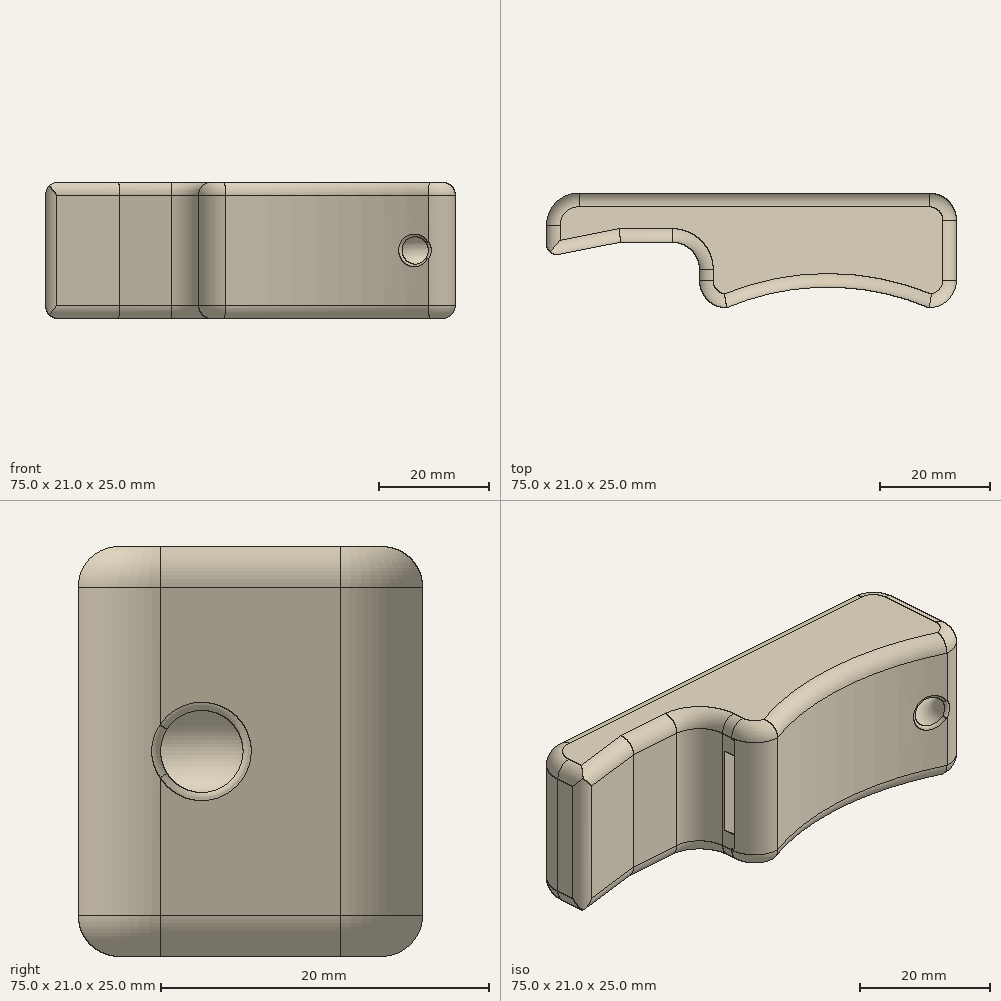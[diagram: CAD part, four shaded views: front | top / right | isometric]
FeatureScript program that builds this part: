
annotation { "Feature Type Name" : "Feature", "Feature Type Description" : "" }
export const myFeature = defineFeature(function(context is Context, id is Id, definition is map)
    precondition{}
    {
        {
            var Q0;
            Q0=qCreatedBy(makeId("Top.planeOp"),FACE);
            var sketch = newSketch(context, id + "F0", { "sketchPlane" : qUnion([Q0])});
            skLineSegment(sketch, "E0", {"start": v(5, -2) * mm, "end": v(5, 0) * mm});
            skPoint(sketch, "E1.visualSharp", {"position": v(0, 0) * mm});
            skArc(sketch, "E1.filletArc", {"start": v(5, 0) * mm, "mid": v(3.54, 3.54) * mm, "end": v(0, 5) * mm});
            skArc(sketch, "E2.filletArc", {"start": v(47, -7) * mm, "mid": v(50.54, -5.54) * mm, "end": v(52, -2) * mm});
            skPoint(sketch, "E3.visualSharp", {"position": v(5, -7) * mm});
            skArc(sketch, "E3.filletArc", {"start": v(5, -2) * mm, "mid": v(6.46, -5.54) * mm, "end": v(10, -7) * mm});
            skLineSegment(sketch, "E4", {"start": v(0, 5) * mm, "end": v(-9.45, 5) * mm});
            skArc(sketch, "E5", {"start": v(-17, 14) * mm, "mid": v(-21.24, 12.24) * mm, "end": v(-23, 8) * mm});
            skLineSegment(sketch, "E6", {"start": v(-23, -19.5) * mm, "end": v(-23, 8) * mm, "construction": true});
            skLineSegment(sketch, "E7", {"start": v(52, -19.5) * mm, "end": v(52, -2) * mm, "construction": true});
            skLineSegment(sketch, "E8", {"start": v(-17, 14) * mm, "end": v(47, 14) * mm});
            skLineSegment(sketch, "E9", {"start": v(52, 9) * mm, "end": v(52, -2) * mm});
            skPoint(sketch, "E10.visualSharp", {"position": v(52, 14) * mm});
            skArc(sketch, "E10.filletArc", {"start": v(52, 9) * mm, "mid": v(50.54, 12.54) * mm, "end": v(47, 14) * mm});
            skArc(sketch, "E11", {"start": v(47, -7) * mm, "mid": v(28.5, -3.21) * mm, "end": v(10, -7) * mm});
            skLineSegment(sketch, "E12", {"start": v(-23, 4.7) * mm, "end": v(-23, 8) * mm});
            skPoint(sketch, "E13.visualSharp", {"position": v(-23, 2.7) * mm});
            skArc(sketch, "E13.filletArc", {"start": v(-23, 4.7) * mm, "mid": v(-22.41, 3.3) * mm, "end": v(-21, 2.7) * mm});
            skLineSegment(sketch, "E14", {"start": v(-21, 2.7) * mm, "end": v(-9.45, 5) * mm});
            skSolve(sketch);
        }
        {
            var Q0;
            Q0=qSketchRegion(id+"F0",true);
            extrude(context, id + "F1", {"entities" : qUnion([Q0]), "endBound" : BoundingType.SYMMETRIC, "depth" : 25 * mm, "offsetDistance" : 25 * mm});
        }
        {
            var Q0;
            Q0=makeQuery(id+"F1.opExtrude","SWEPT_FACE",FACE,{"disambiguationData":[OSD([sQuery(id+"F0.wireOp",EDGE,"E0")])]});
            var sketch = newSketch(context, id + "F2", { "sketchPlane" : qUnion([Q0])});
            skLineSegment(sketch, "E15.bottom", {"start": v(0.5, -9.75) * mm, "end": v(2.5, -9.75) * mm});
            skLineSegment(sketch, "E15.top", {"start": v(0.5, 9.75) * mm, "end": v(2.5, 9.75) * mm});
            skLineSegment(sketch, "E15.left", {"start": v(0.5, -9.75) * mm, "end": v(0.5, 9.75) * mm});
            skLineSegment(sketch, "E15.right", {"start": v(2.5, -9.75) * mm, "end": v(2.5, 9.75) * mm});
            skLineSegment(sketch, "E16", {"start": v(2.5, 12.5) * mm, "end": v(2.5, -12.5) * mm, "construction": true});
            skPoint(sketch, "E17", {"position": v(2.5, 0) * mm});
            skPoint(sketch, "E17.positionSnap0", {"position": v(2.5, 0) * mm});
            skSolve(sketch);
        }
        {
            var Q0;
            Q0=makeQuery(id+"F1.opExtrude","SWEPT_FACE",FACE,{"disambiguationData":[OSD([sQuery(id+"F0.wireOp",EDGE,"E8")])]});
            var sketch = newSketch(context, id + "F3", { "sketchPlane" : qUnion([Q0])});
            skCircle(sketch, "E18", {"center": v(-44.07, 0) * mm, "radius": 3 * mm});
            skPoint(sketch, "E19", {"position": v(-47, 0) * mm});
            skSolve(sketch);
        }
        {
            var Q0;
            Q0=qSketchRegion(id+"F2",true);
            extrude(context, id + "F4", {"entities" : qUnion([Q0]), "operationType" : NewBodyOperationType.REMOVE, "oppositeDirection" : true, "depth" : 16.5 * mm, "offsetDistance" : 25 * mm});
        }
        {
            var Q0;
            Q0=makeQuery(id+"F1.opExtrude","SWEPT_FACE",FACE,{"disambiguationData":[OSD([sQuery(id+"F0.wireOp",EDGE,"E8")])]});
            var sketch = newSketch(context, id + "F5", { "sketchPlane" : qUnion([Q0])});
            skCircle(sketch, "E20", {"center": v(-37.31, 0) * mm, "radius": 1.27 * mm});
            skArc(sketch, "E21", {"start": v(-35.28, 6.05) * mm, "mid": v(-41.7, -4.62) * mm, "end": v(-31.37, 2.34) * mm});
            skArc(sketch, "E22", {"start": v(-37.49, -8.65) * mm, "mid": v(-29.97, -4.58) * mm, "end": v(-29.62, 3.96) * mm});
            skLineSegment(sketch, "E23", {"start": v(-33.52, 7.78) * mm, "end": v(-35.28, 6.05) * mm});
            skLineSegment(sketch, "E24", {"start": v(-29.62, 3.96) * mm, "end": v(-31.37, 2.34) * mm});
            skLineSegment(sketch, "E25", {"start": v(-45.93, -0.75) * mm, "end": v(-45.93, -8.59) * mm});
            skLineSegment(sketch, "E26", {"start": v(-37.49, -8.65) * mm, "end": v(-45.93, -8.59) * mm});
            skArc(sketch, "E27.trimOffspring", {"start": v(-33.52, 7.78) * mm, "mid": v(-42.21, 7.13) * mm, "end": v(-45.93, -0.75) * mm});
            skSolve(sketch);
        }
        {
            var Q0;
            Q0=makeQuery(id+"F5.imprint","IMPRINT",FACE,{"disambiguationData":[TD([[makeQuery(id+"F5.imprint","IMPRINT",EDGE,{"derivedFrom":sQuery(id+"F5.wireOp",EDGE,"E20")}),-1.0]])]});
            var sketch = newSketch(context, id + "F6", { "sketchPlane" : qUnion([Q0])});
            skText(sketch, "E28", { "text": "CORNER", "fontName": "OpenSans-Bold.ttf"});
            skText(sketch, "E29", { "text": "BIKESHOP", "fontName": "OpenSans-Regular.ttf"});
            const initialGuessF6  = {"E28": [-0.02795, 0.00067, 1, 0, 0.00773], "E29": [-0.02795, -0.00678, 1, 0, 0.00678]};
            skSetInitialGuess(sketch, initialGuessF6);
            skSolve(sketch);
        }
        {
            var Q0;
            Q0=makeQuery(id+"F5.imprint","IMPRINT",FACE,{"disambiguationData":[TD([[makeQuery(id+"F5.imprint","IMPRINT",EDGE,{"derivedFrom":sQuery(id+"F5.wireOp",EDGE,"E21")}),-1.0]])]});
            var Q1;
            Q1=qSketchRegion(id+"F6",true);
            var Q2;
            Q2=makeQuery(id+"F5.imprint","IMPRINT",FACE,{"disambiguationData":[TD([[makeQuery(id+"F5.imprint","IMPRINT",EDGE,{"derivedFrom":sQuery(id+"F5.wireOp",EDGE,"E20")}),1.0]])]});
            extrude(context, id + "F7", {"entities" : qUnion([Q0, Q1, Q2]), "operationType" : NewBodyOperationType.REMOVE, "oppositeDirection" : true, "depth" : 3 * mm, "offsetDistance" : 25 * mm});
        }
        {
            var Q0;
            Q0=makeQuery(id+"F4.boolean.opBoolean","COPY",FACE,{"derivedFrom":makeQuery(id+"F4.opExtrude","SWEPT_FACE",FACE,{"disambiguationData":[OSD([sQuery(id+"F2.wireOp",EDGE,"E15.left")])]})});
            var sketch = newSketch(context, id + "F8", { "sketchPlane" : qUnion([Q0])});
            skPoint(sketch, "E30.first.point", {"position": v(21.5, 0) * mm});
            skPoint(sketch, "E30.second.point.positionSnap0", {"position": v(21.5, 0) * mm});
            skLineSegment(sketch, "E31", {"start": v(5, -9.75) * mm, "end": v(21.5, -9.75) * mm});
            skLineSegment(sketch, "E32", {"start": v(21.5, -9.75) * mm, "end": v(21.5, 9.75) * mm});
            skLineSegment(sketch, "E33", {"start": v(21.5, 9.75) * mm, "end": v(5, 9.75) * mm});
            skLineSegment(sketch, "E34", {"start": v(5, 9.75) * mm, "end": v(5, 7.04) * mm});
            skLineSegment(sketch, "E35", {"start": v(5, -9.75) * mm, "end": v(5, -7.04) * mm});
            skArc(sketch, "E36.trimOffspring", {"start": v(5, -7.04) * mm, "mid": v(21.5, 0) * mm, "end": v(5, 7.04) * mm});
            skSolve(sketch);
        }
        {
            var Q0;
            {var subQ0=sQuery(id+"F8.wireOp",EDGE,"E35");Q0=makeQuery(id+"F8.imprint","IMPRINT",FACE,{"disambiguationData":[TD([[makeQuery(id+"F8.imprint","IMPRINT",EDGE,{"derivedFrom":subQ0}),-1.0]])]});}
            var Q1;
            {var subQ0=sQuery(id+"F8.wireOp",EDGE,"E32");var subQ1=sQuery(id+"F8.wireOp",EDGE,"E31");var subQ2=makeQuery(id+"F8.imprint","INTERSECT",VERTEX,{"derivedFrom":[subQ1,subQ0]});Q1=makeQuery(id+"F8.imprint","IMPRINT",FACE,{"disambiguationData":[TD([[makeQuery(id+"F8.imprint","IMPRINT",EDGE,{"disambiguationData":[TD([[subQ2,-1.0]])],"derivedFrom":subQ1}),-1.0]])]});}
            var Q2;
            {var subQ0=sQuery(id+"F8.wireOp",EDGE,"E33");var subQ1=sQuery(id+"F8.wireOp",EDGE,"E32");var subQ2=makeQuery(id+"F8.imprint","INTERSECT",VERTEX,{"derivedFrom":[subQ1,subQ0]});Q2=makeQuery(id+"F8.imprint","IMPRINT",FACE,{"disambiguationData":[TD([[makeQuery(id+"F8.imprint","IMPRINT",EDGE,{"disambiguationData":[TD([[subQ2,1.0]])],"derivedFrom":subQ1}),1.0]])]});}
            var Q3;
            {var subQ0=sQuery(id+"F8.wireOp",EDGE,"E34");Q3=makeQuery(id+"F8.imprint","IMPRINT",FACE,{"disambiguationData":[TD([[makeQuery(id+"F8.imprint","IMPRINT",EDGE,{"derivedFrom":subQ0}),-1.0]])]});}
            extrude(context, id + "F9", {"entities" : qUnion([Q0, Q1, Q2, Q3]), "operationType" : NewBodyOperationType.ADD, "depth" : 2 * mm, "offsetDistance" : 25 * mm});
        }
        {
            var Q0;
            Q0=makeQuery(id+"F1.opExtrude","SWEPT_FACE",FACE,{"disambiguationData":[OSD([sQuery(id+"F0.wireOp",EDGE,"E9")])]});
            var sketch = newSketch(context, id + "F10", { "sketchPlane" : qUnion([Q0])});
            skCircle(sketch, "E37", {"center": v(0.56, 0) * mm, "radius": 2.5 * mm});
            skLineSegment(sketch, "E38", {"start": v(-6.94, 12.64) * mm, "end": v(-6.94, -12.58) * mm});
            skLineSegment(sketch, "E39", {"start": v(-1.94, 0) * mm, "end": v(-6.94, 0) * mm});
            skSolve(sketch);
        }
        {
            var Q0;
            Q0=makeQuery(id+"F10.imprint","IMPRINT",FACE,{"disambiguationData":[TD([[makeQuery(id+"F10.imprint","IMPRINT",EDGE,{"derivedFrom":sQuery(id+"F10.wireOp",EDGE,"E37")}),1.0]])]});
            var Q1;
            Q1=sQuery(id+"F10.wireOp",EDGE,"E38");
            revolve(context, id + "F11", {"operationType" : NewBodyOperationType.REMOVE, "entities" : qUnion([Q0]), "axis" : qUnion([Q1]), "revolveType" : RevolveType.FULL, "oppositeDirection" : true});
        }
        {
            var Q0;
            Q0=makeQuery(id+"F1.opExtrude","CAP_EDGE",EDGE,{"disambiguationData":[OSD([sQuery(id+"F0.wireOp",EDGE,"E8")])],"isStart":true});
            var Q1;
            Q1=makeQuery(id+"F1.opExtrude","CAP_EDGE",EDGE,{"disambiguationData":[OSD([sQuery(id+"F0.wireOp",EDGE,"E9")])],"isStart":true});
            var Q2;
            Q2=makeQuery(id+"F1.opExtrude","CAP_EDGE",EDGE,{"disambiguationData":[OSD([sQuery(id+"F0.wireOp",EDGE,"E11")])],"isStart":true});
            var Q3;
            Q3=makeQuery(id+"F1.opExtrude","CAP_EDGE",EDGE,{"disambiguationData":[OSD([sQuery(id+"F0.wireOp",EDGE,"E1.filletArc")])],"isStart":true});
            var Q4;
            Q4=makeQuery(id+"F1.opExtrude","CAP_EDGE",EDGE,{"disambiguationData":[OSD([sQuery(id+"F0.wireOp",EDGE,"E4")])],"isStart":true});
            var Q5;
            Q5=makeQuery(id+"F1.opExtrude","CAP_EDGE",EDGE,{"disambiguationData":[OSD([sQuery(id+"F0.wireOp",EDGE,"E14")])],"isStart":true});
            var Q6;
            Q6=makeQuery(id+"F1.opExtrude","CAP_EDGE",EDGE,{"disambiguationData":[OSD([sQuery(id+"F0.wireOp",EDGE,"E12")])],"isStart":true});
            var Q7;
            Q7=makeQuery(id+"F1.opExtrude","CAP_EDGE",EDGE,{"disambiguationData":[OSD([sQuery(id+"F0.wireOp",EDGE,"E5")])],"isStart":true});
            var Q8;
            Q8=makeQuery(id+"F1.opExtrude","CAP_EDGE",EDGE,{"disambiguationData":[OSD([sQuery(id+"F0.wireOp",EDGE,"E0")])],"isStart":true});
            var Q9;
            Q9=makeQuery(id+"F1.opExtrude","CAP_EDGE",EDGE,{"disambiguationData":[OSD([sQuery(id+"F0.wireOp",EDGE,"E3.filletArc")])],"isStart":true});
            var Q10;
            Q10=makeQuery(id+"F1.opExtrude","CAP_EDGE",EDGE,{"disambiguationData":[OSD([sQuery(id+"F0.wireOp",EDGE,"E2.filletArc")])],"isStart":true});
            var Q11;
            Q11=makeQuery(id+"F1.opExtrude","CAP_EDGE",EDGE,{"disambiguationData":[OSD([sQuery(id+"F0.wireOp",EDGE,"E10.filletArc")])],"isStart":true});
            var Q12;
            Q12=makeQuery(id+"F1.opExtrude","CAP_EDGE",EDGE,{"disambiguationData":[OSD([sQuery(id+"F0.wireOp",EDGE,"E9")])],"isStart":false});
            var Q13;
            Q13=makeQuery(id+"F1.opExtrude","CAP_EDGE",EDGE,{"disambiguationData":[OSD([sQuery(id+"F0.wireOp",EDGE,"E11")])],"isStart":false});
            var Q14;
            Q14=makeQuery(id+"F1.opExtrude","CAP_EDGE",EDGE,{"disambiguationData":[OSD([sQuery(id+"F0.wireOp",EDGE,"E2.filletArc")])],"isStart":false});
            var Q15;
            Q15=makeQuery(id+"F1.opExtrude","CAP_EDGE",EDGE,{"disambiguationData":[OSD([sQuery(id+"F0.wireOp",EDGE,"E10.filletArc")])],"isStart":false});
            var Q16;
            Q16=makeQuery(id+"F1.opExtrude","CAP_EDGE",EDGE,{"disambiguationData":[OSD([sQuery(id+"F0.wireOp",EDGE,"E8")])],"isStart":false});
            var Q17;
            Q17=makeQuery(id+"F1.opExtrude","CAP_EDGE",EDGE,{"disambiguationData":[OSD([sQuery(id+"F0.wireOp",EDGE,"E5")])],"isStart":false});
            var Q18;
            Q18=makeQuery(id+"F1.opExtrude","CAP_EDGE",EDGE,{"disambiguationData":[OSD([sQuery(id+"F0.wireOp",EDGE,"E14")])],"isStart":false});
            var Q19;
            Q19=makeQuery(id+"F1.opExtrude","CAP_EDGE",EDGE,{"disambiguationData":[OSD([sQuery(id+"F0.wireOp",EDGE,"E4")])],"isStart":false});
            var Q20;
            Q20=makeQuery(id+"F1.opExtrude","CAP_EDGE",EDGE,{"disambiguationData":[OSD([sQuery(id+"F0.wireOp",EDGE,"E1.filletArc")])],"isStart":false});
            var Q21;
            Q21=makeQuery(id+"F1.opExtrude","CAP_EDGE",EDGE,{"disambiguationData":[OSD([sQuery(id+"F0.wireOp",EDGE,"E3.filletArc")])],"isStart":false});
            var Q22;
            Q22=makeQuery(id+"F1.opExtrude","CAP_EDGE",EDGE,{"disambiguationData":[OSD([sQuery(id+"F0.wireOp",EDGE,"E0")])],"isStart":false});
            var Q23;
            Q23=makeQuery(id+"F1.opExtrude","CAP_EDGE",EDGE,{"disambiguationData":[OSD([sQuery(id+"F0.wireOp",EDGE,"E12")])],"isStart":false});
            fillet(context, id + "F12", {"entities" : qUnion([Q0, Q1, Q2, Q3, Q4, Q5, Q6, Q7, Q8, Q9, Q10, Q11, Q12, Q13, Q14, Q15, Q16, Q17, Q18, Q19, Q20, Q21, Q22, Q23]), "radius" : 2.5 * mm, "allowEdgeOverflow" : false});
        }
        {
            var Q0;
            Q0=makeQuery(id+"F11.boolean.opBoolean","INTERSECT",EDGE,{"derivedFrom":[makeQuery(id+"F1.opExtrude","SWEPT_FACE",FACE,{"disambiguationData":[OSD([sQuery(id+"F0.wireOp",EDGE,"E9")])]}),makeQuery(id+"F11.opRevolve","SWEPT_FACE",FACE,{"disambiguationData":[OSD([sQuery(id+"F10.wireOp",EDGE,"E37")])]})]});
            var Q1;
            Q1=makeQuery(id+"F11.boolean.opBoolean","INTERSECT",EDGE,{"derivedFrom":[makeQuery(id+"F1.opExtrude","SWEPT_FACE",FACE,{"disambiguationData":[OSD([sQuery(id+"F0.wireOp",EDGE,"E11")])]}),makeQuery(id+"F11.opRevolve","SWEPT_FACE",FACE,{"disambiguationData":[OSD([sQuery(id+"F10.wireOp",EDGE,"E37")])]})]});
            var Q2;
            Q2=makeQuery(id+"F11.boolean.opBoolean","INTERSECT",EDGE,{"derivedFrom":[makeQuery(id+"F1.opExtrude","SWEPT_FACE",FACE,{"disambiguationData":[OSD([sQuery(id+"F0.wireOp",EDGE,"E2.filletArc")])]}),makeQuery(id+"F11.opRevolve","SWEPT_FACE",FACE,{"disambiguationData":[OSD([sQuery(id+"F10.wireOp",EDGE,"E37")])]})]});
            var Q3;
            Q3=makeQuery(id+"F11.boolean.opBoolean","COPY",FACE,{"derivedFrom":makeQuery(id+"F11.opRevolve","SWEPT_FACE",FACE,{"disambiguationData":[OSD([sQuery(id+"F10.wireOp",EDGE,"E37")])]})});
            fillet(context, id + "F13", {"entities" : qUnion([Q0, Q1, Q2, Q3]), "radius" : .5 * mm, "tangentPropagation" : true, "allowEdgeOverflow" : false});
        }
    });
